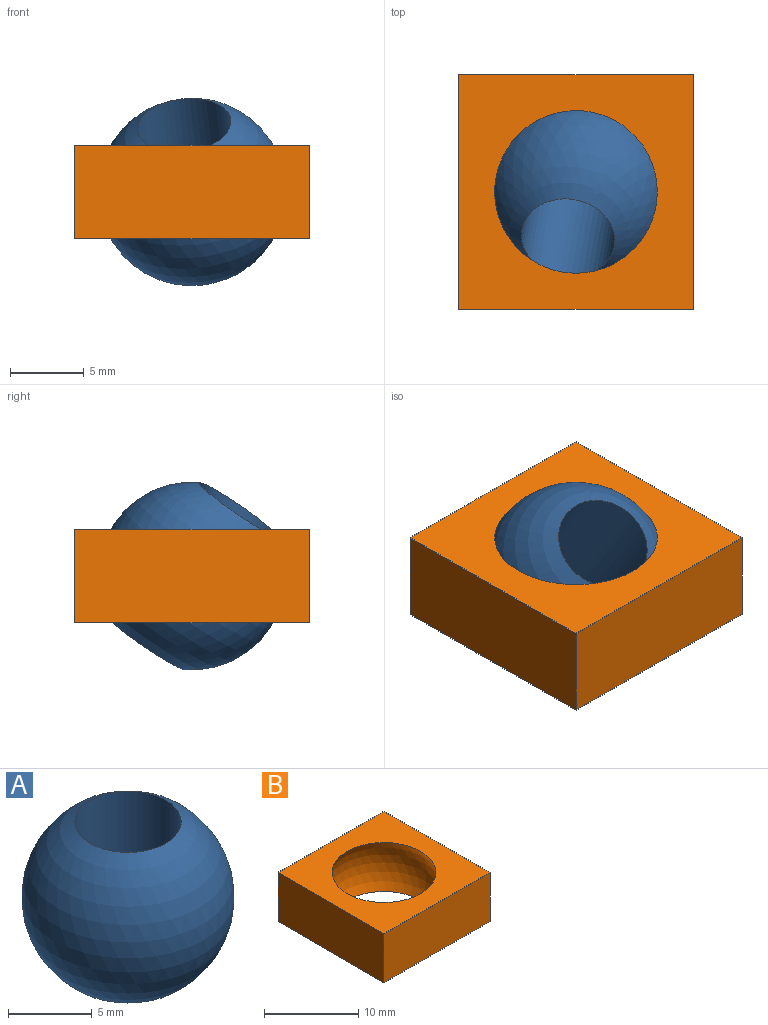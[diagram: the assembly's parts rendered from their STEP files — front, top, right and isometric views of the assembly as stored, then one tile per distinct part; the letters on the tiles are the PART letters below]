
ASSEMBLY  parts=2 mates=1
PART A: 2 faces, bbox 12.7x12.7x11 mm
  f0: sphere r=6.35mm, area 438.8mm2, adj f1
  f1: cylinder r=3.17mm len=11mm, axis (0,0,1), area 219.4mm2, adj f0
PART B: 7 faces, bbox 15.9x15.9x6.4 mm
  f0: plane 15.88x6.35mm, normal (0,-1,0), area 100.8mm2, adj f1,f3,f4,f5
  f1: plane 15.88x6.35mm, normal (1,0,0), area 100.8mm2, adj f0,f2,f4,f5
  f2: plane 15.88x6.35mm, normal (0,1,0), area 100.8mm2, adj f1,f3,f4,f5
  f3: plane 15.88x6.35mm, normal (-1,0,0), area 100.8mm2, adj f0,f2,f4,f5
  f4: plane 15.88x15.88mm, normal (0,0,1), area 157mm2, adj f0,f1,f2,f3,f6
  f5: plane 15.88x15.88mm, normal (0,0,-1), area 157mm2, adj f0,f1,f2,f3,f6
  f6: sphere r=6.35mm, area 253.4mm2, adj f4,f5
PLACE A rot(axis=(0.41,-0.34,0.85),68.8deg) t=(0,0,0)mm
PLACE B at identity fixed
MATE ball B.f6 <-> A.f1  axis (0,0,1) through (0,0,0)mm
